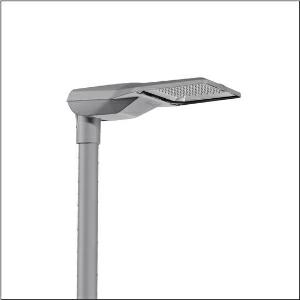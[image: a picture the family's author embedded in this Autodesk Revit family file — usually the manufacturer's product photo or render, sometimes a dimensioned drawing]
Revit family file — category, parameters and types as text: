
# Revit family: streetlight_sl_21_iq_midi___st1_5a_5xe3p31d08mb_51c0
name_source: partatom
category: Lighting Fixtures
units: mm (PartAtom-declared; Revit-internal decimal feet)

## family parameters
Cut with Voids When Loaded = No
Host = Face
Light Source = No
Part Type = Normal
Room Calculation Point = No
Round Connector Dimension = Use Diameter
Shared = No

## types (1)
- --- (1 x LED, 19170 lm, 146.7 W, 3000K)
    Apparent Load = 147 VA
    CIE Flux Codes = 22 53 95 100 100
    Color Rendering = 70
    Color Temperature = 3000K
    Default Elevation = 1800 mm
    Description = Streetlight SL 21 iQ midi, mast luminaire, primary light control with lens, of PMMA, primary optical cover: cover, of toughened safety glass, transparent, light distribution: ST1.5a, light emission: direct distribution, primary light characteristic: asymmetric, installation type: post-top, side-entry, LED, High Power LED, rated luminous flux: 19.170lm, luminous efficacy: 131lm/W, light colour: 730, colour temperature: 3000K, control: Auto-Match, Temp-Guard, Lumen-Switch, Night-Set, Smart-Wire, Light-Fading, Desk-Remote (wireless, voltage-free reading and setting of iQ features in the workshop via application-optimized NFC function/RFID function), optimised constant luminous flux control (CLO 2.0), pre-setting: linear dimming characteristic, mains connection: 230..240V, AC, 50/60Hz, start of lifetime: 147W, end of service life: 161W, reduction: 62W, luminaire housing, of diecast aluminium, powder-coated, Siteco® metallic grey (DB 702S), corrosivity category C5 mid according to DIN EN ISO 12944, please order mast flange separately, inclination adjustable: 0°, 5°, 10°, 15°, sealing non-destructively replaceable, multi-level sealing system, length: 644mm, width: 335mm, height: 110mm, mast flange for spigot size: 42mm (side-entry): 5XC10008XM4, 60/48mm (side-entry/post-top): 5XC10108XM2, 76/60mm (side-entry/post-top): 5XC10108XM1, protection rating (complete): IP66, insulation class (complete): insulation class II (safety insulation), certification: CE, ENEC, ENEC+, VDE, impact resistance: IK09, permissible operating ambient temperature for outdoor applications: -40..+50°C, standard-compliant lighting for roads and squares, packaging unit: 1 piece

Light Distribution: ST1.5a
    Height = 111 mm
    Lamp = 1 x LED
    Lamp Light Flux = 19170 lm
    Lamp Power = 146.7 W
    Lamp count = 1
    Length = 644 mm
    Luminous efficacy = 131 lm/W
    Manufacturer = Siteco
    ModVariant = No
    Model = 5XE3P31D08MB
    Number of Poles = 1
    OnlyDefault = Yes
    Power Factor = 1
    Product Name = Streetlight SL 21 iQ midi | ST1.5a
    Product group = mast luminaire | pylon top
    ProductGroupID = 6100
    Protection Class = Protection class II
    Protection Degree = IP 66
    RLX_Detail_Level = 1
    RLX_Emergency_Light_Flux = 0 lm
    RLX_Emergency_Type = 0
    RLX_Emergency_Type_DB = No
    RlxData = <blob elided: 94205 chars, md5=8e618315>
    Socket = socket
    Standby Power = 0 W
    System Light Flux = 19169 lm
    System Power = 147 W
    Type Comments = factory setting: luminous flux: 100 % | dim-lin: 254 | 753 mA
    Type Image = l_1004298.jpg
    URL = http://relux.com
    VarID = @adj_147589
    Voltage = 0 V
    Weight = 0.00 kg
    Width = 336 mm

## geometry (parser evidence)
native form markers: Blend x4, Sweep x12
no freeform markers — native parametric forms only
